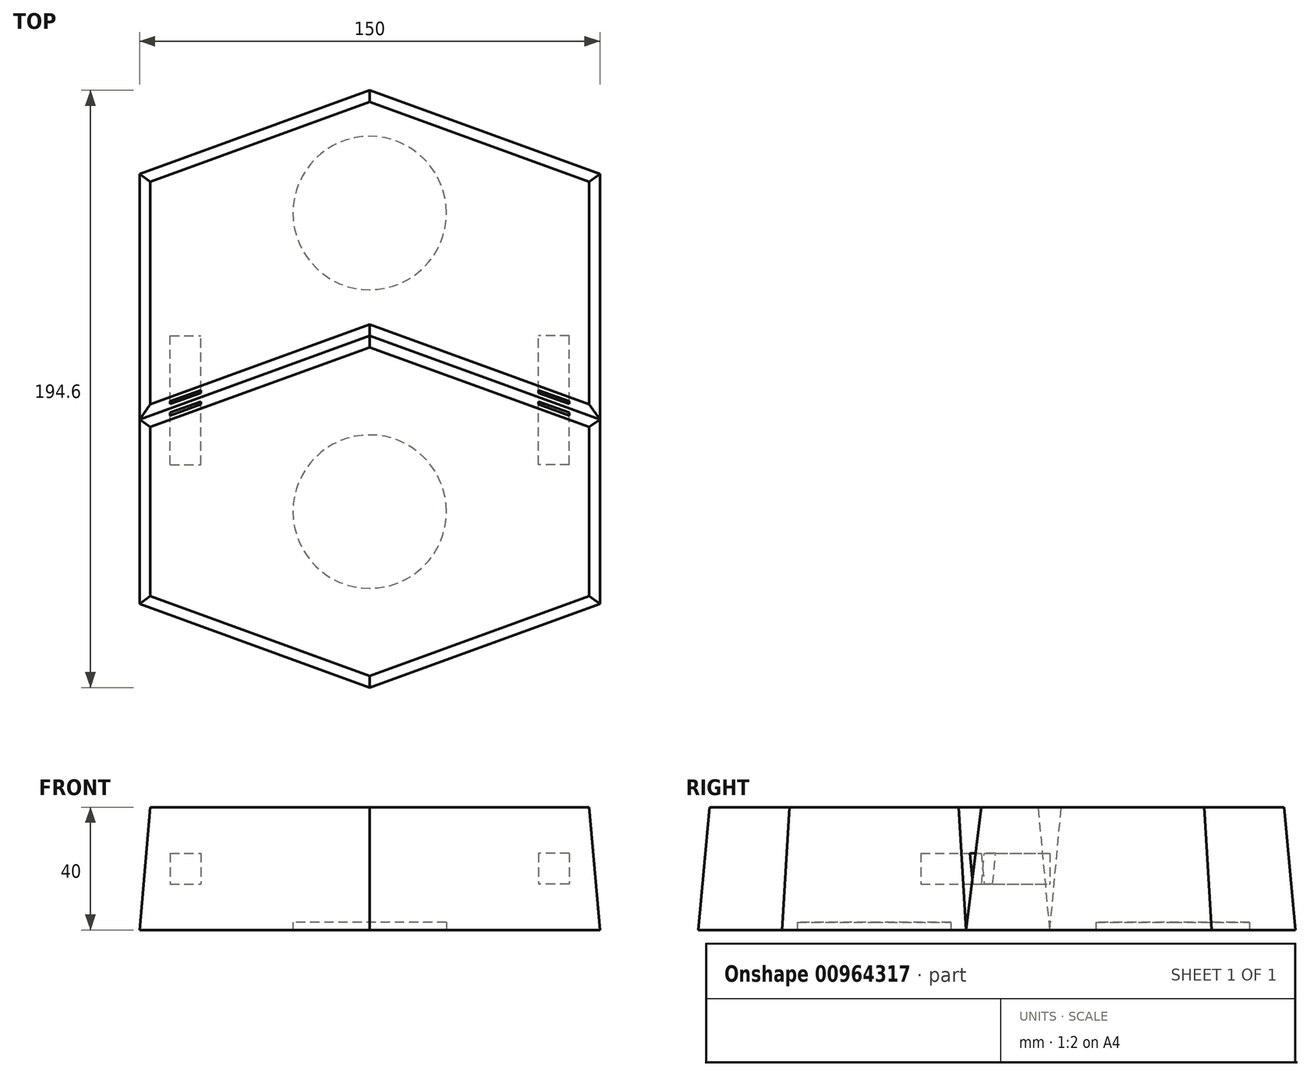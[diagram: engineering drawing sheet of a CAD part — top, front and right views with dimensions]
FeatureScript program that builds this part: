
annotation { "Feature Type Name" : "Feature", "Feature Type Description" : "" }
export const myFeature = defineFeature(function(context is Context, id is Id, definition is map)
    precondition{}
    {
        {
            var Q0;
            Q0=qCreatedBy(makeId("Top.planeOp"),FACE);
            var sketch = newSketch(context, id + "F0", { "sketchPlane" : qUnion([Q0])});
            skLineSegment(sketch, "E0", {"start": v(-75, 52.7) * mm, "end": v(-75, -27.3) * mm});
            skLineSegment(sketch, "E1", {"start": v(-75, -27.3) * mm, "end": v(0, 0) * mm});
            skLineSegment(sketch, "E2", {"start": v(0, 0) * mm, "end": v(0, 80) * mm, "construction": true});
            skLineSegment(sketch, "E3", {"start": v(0, 80) * mm, "end": v(-75, 52.7) * mm});
            skLineSegment(sketch, "E4", {"start": v(-75, -27.3) * mm, "end": v(-75, -87.3) * mm});
            skLineSegment(sketch, "E5", {"start": v(-75, -87.3) * mm, "end": v(0, -114.6) * mm});
            skLineSegment(sketch, "E6", {"start": v(0, -114.6) * mm, "end": v(0, 0) * mm, "construction": true});
            skLineSegment(sketch, "E7.MirrorCS", {"start": v(0, 80) * mm, "end": v(75, 52.7) * mm});
            skLineSegment(sketch, "E8.MirrorCS", {"start": v(75, 52.7) * mm, "end": v(75, -27.3) * mm});
            skLineSegment(sketch, "E9.MirrorCS", {"start": v(75, -27.3) * mm, "end": v(0, 0) * mm});
            skLineSegment(sketch, "E10.MirrorCS", {"start": v(75, -87.3) * mm, "end": v(0, -114.6) * mm});
            skLineSegment(sketch, "E11.MirrorCS", {"start": v(75, -27.3) * mm, "end": v(75, -87.3) * mm});
            skCircle(sketch, "E12", {"center": v(0, 40) * mm, "radius": 25 * mm});
            skCircle(sketch, "E13", {"center": v(0, -57.3) * mm, "radius": 25 * mm});
            skSolve(sketch);
        }
        {
            var Q0;
            Q0=makeQuery(id+"F0.imprint","IMPRINT",FACE,{"disambiguationData":[TD([[makeQuery(id+"F0.imprint","IMPRINT",EDGE,{"derivedFrom":sQuery(id+"F0.wireOp",EDGE,"E0")}),1.0]])]});
            var Q1;
            Q1=makeQuery(id+"F0.imprint","IMPRINT",FACE,{"disambiguationData":[TD([[makeQuery(id+"F0.imprint","IMPRINT",EDGE,{"derivedFrom":sQuery(id+"F0.wireOp",EDGE,"E12")}),1.0]])]});
            extrude(context, id + "F1", {"entities" : qUnion([Q0, Q1]), "depth" : 40 * mm, "offsetDistance" : 25 * mm, "hasDraft" : true, "draftAngle" : 5 * degree, "draftPullDirection" : true});
        }
        {
            var Q0;
            Q0=makeQuery(id+"F0.imprint","IMPRINT",FACE,{"disambiguationData":[TD([[makeQuery(id+"F0.imprint","IMPRINT",EDGE,{"derivedFrom":sQuery(id+"F0.wireOp",EDGE,"E1")}),-1.0]])]});
            var Q1;
            Q1=makeQuery(id+"F0.imprint","IMPRINT",FACE,{"disambiguationData":[TD([[makeQuery(id+"F0.imprint","IMPRINT",EDGE,{"derivedFrom":sQuery(id+"F0.wireOp",EDGE,"E13")}),1.0]])]});
            extrude(context, id + "F2", {"entities" : qUnion([Q0, Q1]), "depth" : 40 * mm, "offsetDistance" : 25 * mm, "hasDraft" : true, "draftAngle" : 5 * degree, "draftPullDirection" : true});
        }
        {
            var Q0;
            Q0=makeQuery(id+"F0.imprint","IMPRINT",FACE,{"disambiguationData":[TD([[makeQuery(id+"F0.imprint","IMPRINT",EDGE,{"derivedFrom":sQuery(id+"F0.wireOp",EDGE,"E12")}),1.0]])]});
            var Q1;
            Q1=makeQuery(id+"F0.imprint","IMPRINT",FACE,{"disambiguationData":[TD([[makeQuery(id+"F0.imprint","IMPRINT",EDGE,{"derivedFrom":sQuery(id+"F0.wireOp",EDGE,"E13")}),1.0]])]});
            extrude(context, id + "F3", {"entities" : qUnion([Q0, Q1]), "operationType" : NewBodyOperationType.REMOVE, "depth" : 2.5 * mm, "offsetDistance" : 25 * mm});
        }
        {
            var Q0;
            Q0=qCreatedBy(makeId("Front.planeOp"),FACE);
            var sketch = newSketch(context, id + "F4", { "sketchPlane" : qUnion([Q0])});
            skLineSegment(sketch, "E14.bottom", {"start": v(-65, 25) * mm, "end": v(-55, 25) * mm});
            skLineSegment(sketch, "E14.top", {"start": v(-65, 15) * mm, "end": v(-55, 15) * mm});
            skLineSegment(sketch, "E14.left", {"start": v(-65, 25) * mm, "end": v(-65, 15) * mm});
            skLineSegment(sketch, "E14.right", {"start": v(-55, 25) * mm, "end": v(-55, 15) * mm});
            skLineSegment(sketch, "E15.MirrorCS", {"start": v(55, 25) * mm, "end": v(55, 15) * mm});
            skLineSegment(sketch, "E16.MirrorCS", {"start": v(65, 25) * mm, "end": v(55, 25) * mm});
            skLineSegment(sketch, "E17.MirrorCS", {"start": v(65, 15) * mm, "end": v(55, 15) * mm});
            skLineSegment(sketch, "E18.MirrorCS", {"start": v(65, 25) * mm, "end": v(65, 15) * mm});
            skSolve(sketch);
        }
        {
            var Q0;
            Q0 = qSketchRegion(id + "F4", true);
            extrude(context, id + "F5", {"entities" : qUnion([Q0]), "operationType" : NewBodyOperationType.REMOVE, "depth" : 42 * mm, "offsetDistance" : 25 * mm});
        }
    });
